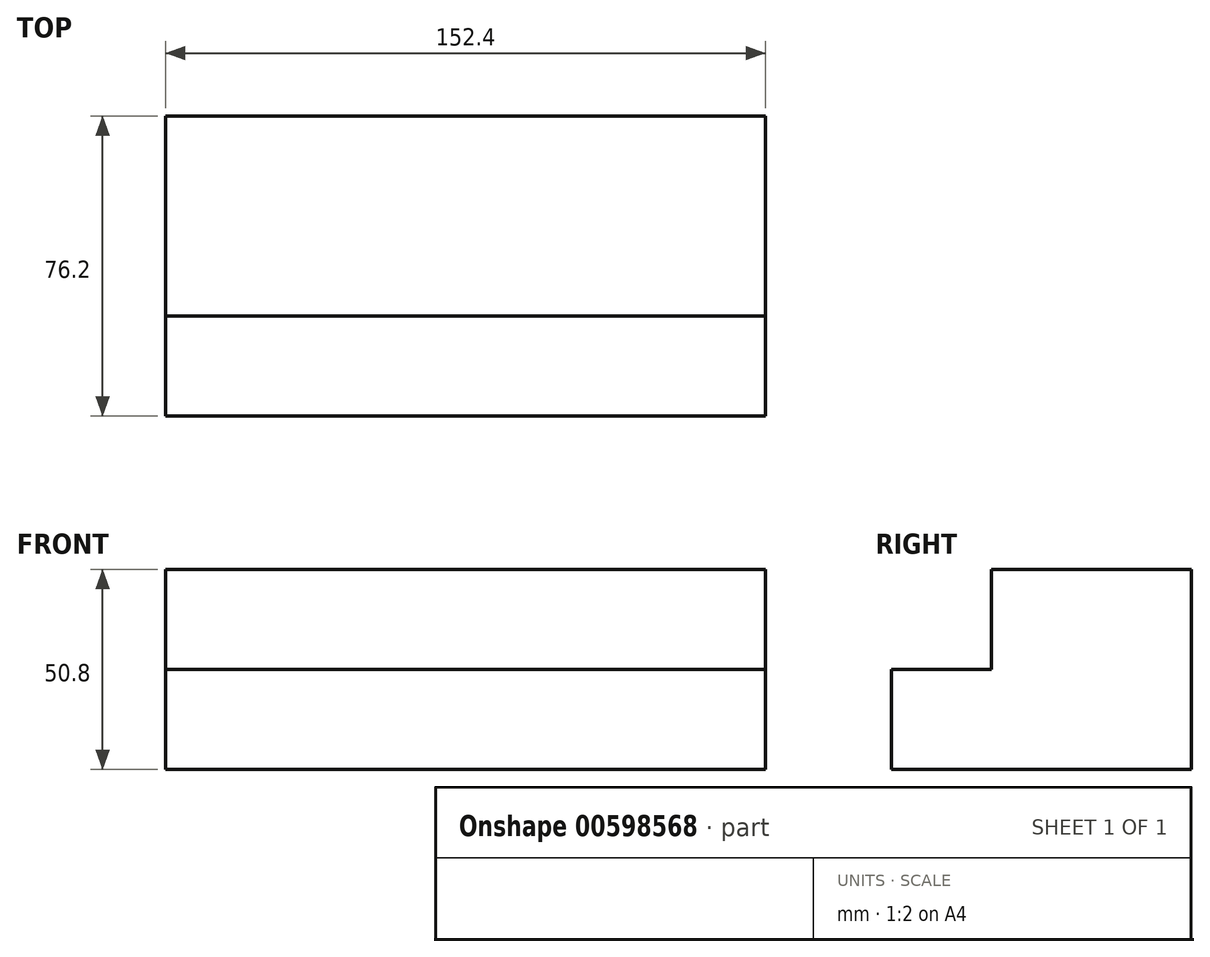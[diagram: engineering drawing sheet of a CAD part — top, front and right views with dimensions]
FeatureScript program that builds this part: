
annotation { "Feature Type Name" : "Feature", "Feature Type Description" : "" }
export const myFeature = defineFeature(function(context is Context, id is Id, definition is map)
    precondition{}
    {
        {
            var Q0;
            Q0=qCreatedBy(makeId("Right.planeOp"),FACE);
            var sketch = newSketch(context, id + "F0", { "sketchPlane" : qUnion([Q0])});
            skLineSegment(sketch, "E0", {"start": v(0, 0) * mm, "end": v(-25.4, 0) * mm});
            skLineSegment(sketch, "E1", {"start": v(-25.4, 0) * mm, "end": v(-25.4, 25.4) * mm});
            skLineSegment(sketch, "E2", {"start": v(-25.4, 25.4) * mm, "end": v(0, 25.4) * mm});
            skLineSegment(sketch, "E3", {"start": v(0, 25.4) * mm, "end": v(0, 50.8) * mm});
            skLineSegment(sketch, "E4", {"start": v(0, 50.8) * mm, "end": v(50.8, 50.8) * mm});
            skLineSegment(sketch, "E5", {"start": v(50.8, 50.8) * mm, "end": v(50.8, 0) * mm});
            skLineSegment(sketch, "E6", {"start": v(50.8, 0) * mm, "end": v(0, 0) * mm});
            skSolve(sketch);
        }
        {
            var Q0;
            Q0 = qSketchRegion(id + "F0", true);
            extrude(context, id + "F1", {"entities" : qUnion([Q0]), "depth" : 152.4 * mm, "offsetDistance" : 25.4 * mm});
        }
    });
